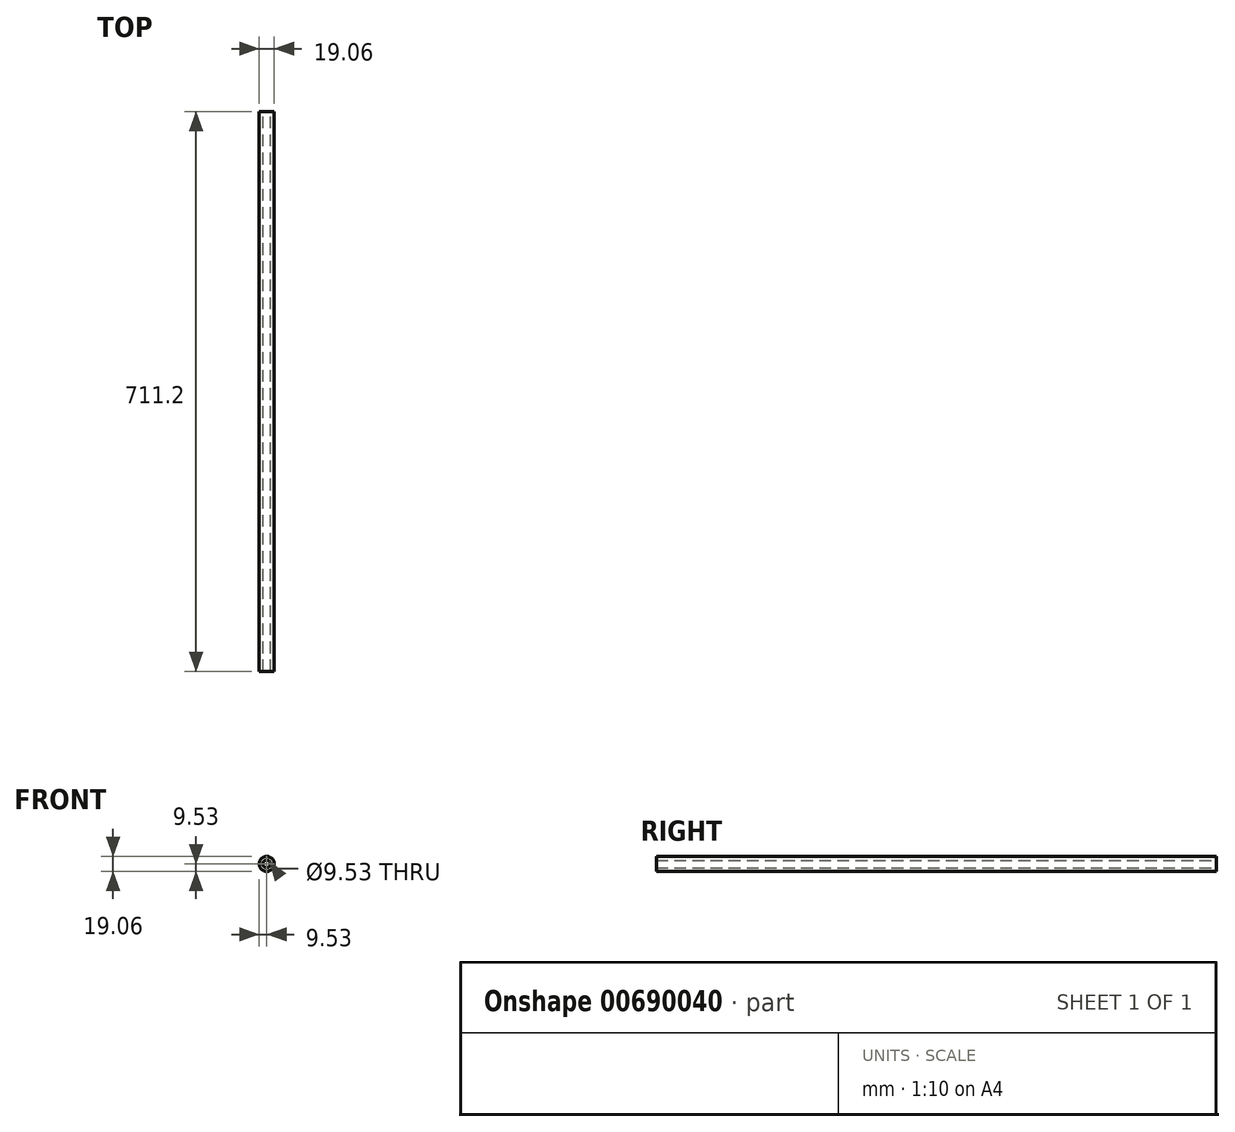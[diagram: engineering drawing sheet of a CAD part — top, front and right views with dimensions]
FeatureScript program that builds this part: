
annotation { "Feature Type Name" : "Feature", "Feature Type Description" : "" }
export const myFeature = defineFeature(function(context is Context, id is Id, definition is map)
    precondition{}
    {
        {
            var Q0;
            Q0=qCreatedBy(makeId("Front.planeOp"),FACE);
            var sketch = newSketch(context, id + "F0", { "sketchPlane" : qUnion([Q0])});
            skCircle(sketch, "E0", {"center": v(0, 0) * mm, "radius": 9.53 * mm});
            skCircle(sketch, "E1", {"center": v(0, 0) * mm, "radius": 4.76 * mm});
            skSolve(sketch);
        }
        {
            var Q0;
            Q0 = qSketchRegion(id + "F0", true);
            extrude(context, id + "F1", {"entities" : qUnion([Q0]), "depth" : 711.2 * mm, "offsetDistance" : 25.4 * mm});
        }
    });
